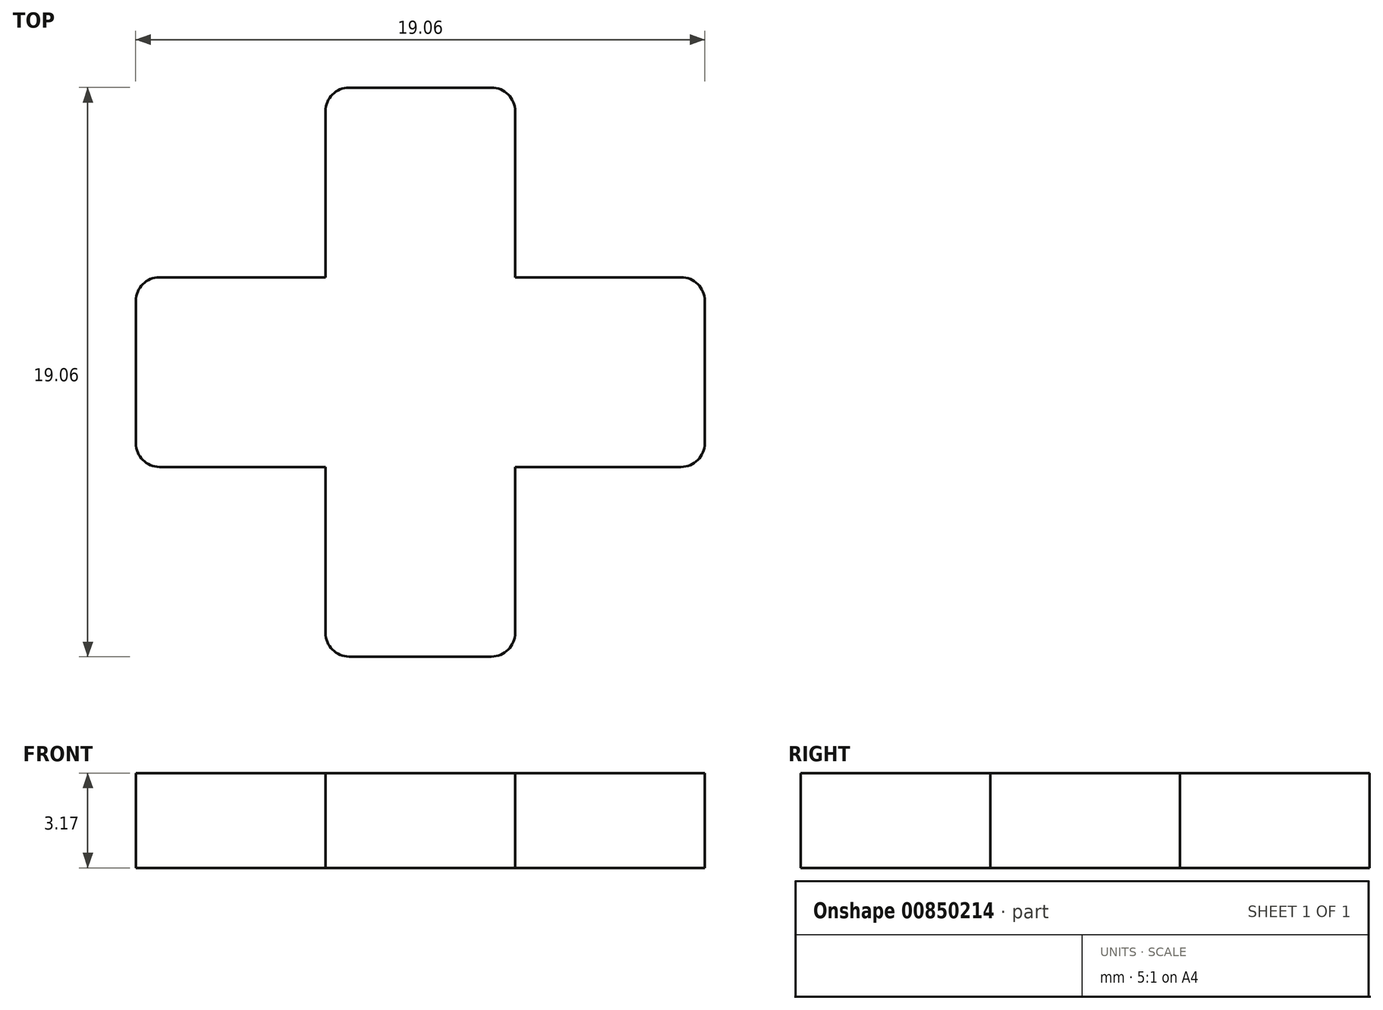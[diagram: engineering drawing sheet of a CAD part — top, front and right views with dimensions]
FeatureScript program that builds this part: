
annotation { "Feature Type Name" : "Feature", "Feature Type Description" : "" }
export const myFeature = defineFeature(function(context is Context, id is Id, definition is map)
    precondition{}
    {
        {
            var Q0;
            Q0=qCreatedBy(makeId("Top.planeOp"),FACE);
            var sketch = newSketch(context, id + "F0", { "sketchPlane" : qUnion([Q0])});
            skLineSegment(sketch, "E0.bottom", {"start": v(-2.38, 9.52) * mm, "end": v(2.38, 9.52) * mm});
            skLineSegment(sketch, "E0.top", {"start": v(-2.38, -9.53) * mm, "end": v(2.38, -9.53) * mm});
            skLineSegment(sketch, "E0.left", {"start": v(-3.17, 8.73) * mm, "end": v(-3.17, -8.73) * mm});
            skLineSegment(sketch, "E0.right", {"start": v(3.18, 8.73) * mm, "end": v(3.18, -8.73) * mm});
            skPoint(sketch, "E0.middle", {"position": v(0, 0) * mm});
            skLineSegment(sketch, "E1.bottom", {"start": v(8.73, 3.18) * mm, "end": v(-8.73, 3.18) * mm});
            skLineSegment(sketch, "E1.top", {"start": v(8.73, -3.18) * mm, "end": v(-8.73, -3.18) * mm});
            skLineSegment(sketch, "E1.left", {"start": v(9.53, 2.38) * mm, "end": v(9.53, -2.38) * mm});
            skLineSegment(sketch, "E1.right", {"start": v(-9.52, 2.38) * mm, "end": v(-9.52, -2.38) * mm});
            skPoint(sketch, "E2.visualSharp", {"position": v(-3.17, 9.52) * mm});
            skArc(sketch, "E2.filletArc", {"start": v(-2.38, 9.52) * mm, "mid": v(-2.94, 9.3) * mm, "end": v(-3.17, 8.73) * mm});
            skPoint(sketch, "E3.visualSharp", {"position": v(3.18, 9.52) * mm});
            skArc(sketch, "E3.filletArc", {"start": v(3.18, 8.73) * mm, "mid": v(2.94, 9.3) * mm, "end": v(2.38, 9.52) * mm});
            skPoint(sketch, "E4.visualSharp", {"position": v(9.53, 3.18) * mm});
            skArc(sketch, "E4.filletArc", {"start": v(9.53, 2.38) * mm, "mid": v(9.3, 2.94) * mm, "end": v(8.73, 3.18) * mm});
            skPoint(sketch, "E5.visualSharp", {"position": v(9.53, -3.18) * mm});
            skArc(sketch, "E5.filletArc", {"start": v(8.73, -3.18) * mm, "mid": v(9.3, -2.94) * mm, "end": v(9.53, -2.38) * mm});
            skPoint(sketch, "E6.visualSharp", {"position": v(3.18, -9.53) * mm});
            skArc(sketch, "E6.filletArc", {"start": v(2.38, -9.53) * mm, "mid": v(2.94, -9.3) * mm, "end": v(3.18, -8.73) * mm});
            skPoint(sketch, "E7.visualSharp", {"position": v(-3.17, -9.53) * mm});
            skArc(sketch, "E7.filletArc", {"start": v(-3.17, -8.73) * mm, "mid": v(-2.94, -9.3) * mm, "end": v(-2.38, -9.53) * mm});
            skPoint(sketch, "E8.visualSharp", {"position": v(-9.52, -3.18) * mm});
            skArc(sketch, "E8.filletArc", {"start": v(-9.52, -2.38) * mm, "mid": v(-9.3, -2.94) * mm, "end": v(-8.73, -3.18) * mm});
            skPoint(sketch, "E9.visualSharp", {"position": v(-9.52, 3.18) * mm});
            skArc(sketch, "E9.filletArc", {"start": v(-8.73, 3.18) * mm, "mid": v(-9.3, 2.94) * mm, "end": v(-9.52, 2.38) * mm});
            skSolve(sketch);
        }
        {
            var Q0;
            Q0 = qSketchRegion(id + "F0", true);
            extrude(context, id + "F1", {"entities" : qUnion([Q0]), "depth" : 3.17 * mm, "offsetDistance" : 25.4 * mm});
        }
    });
